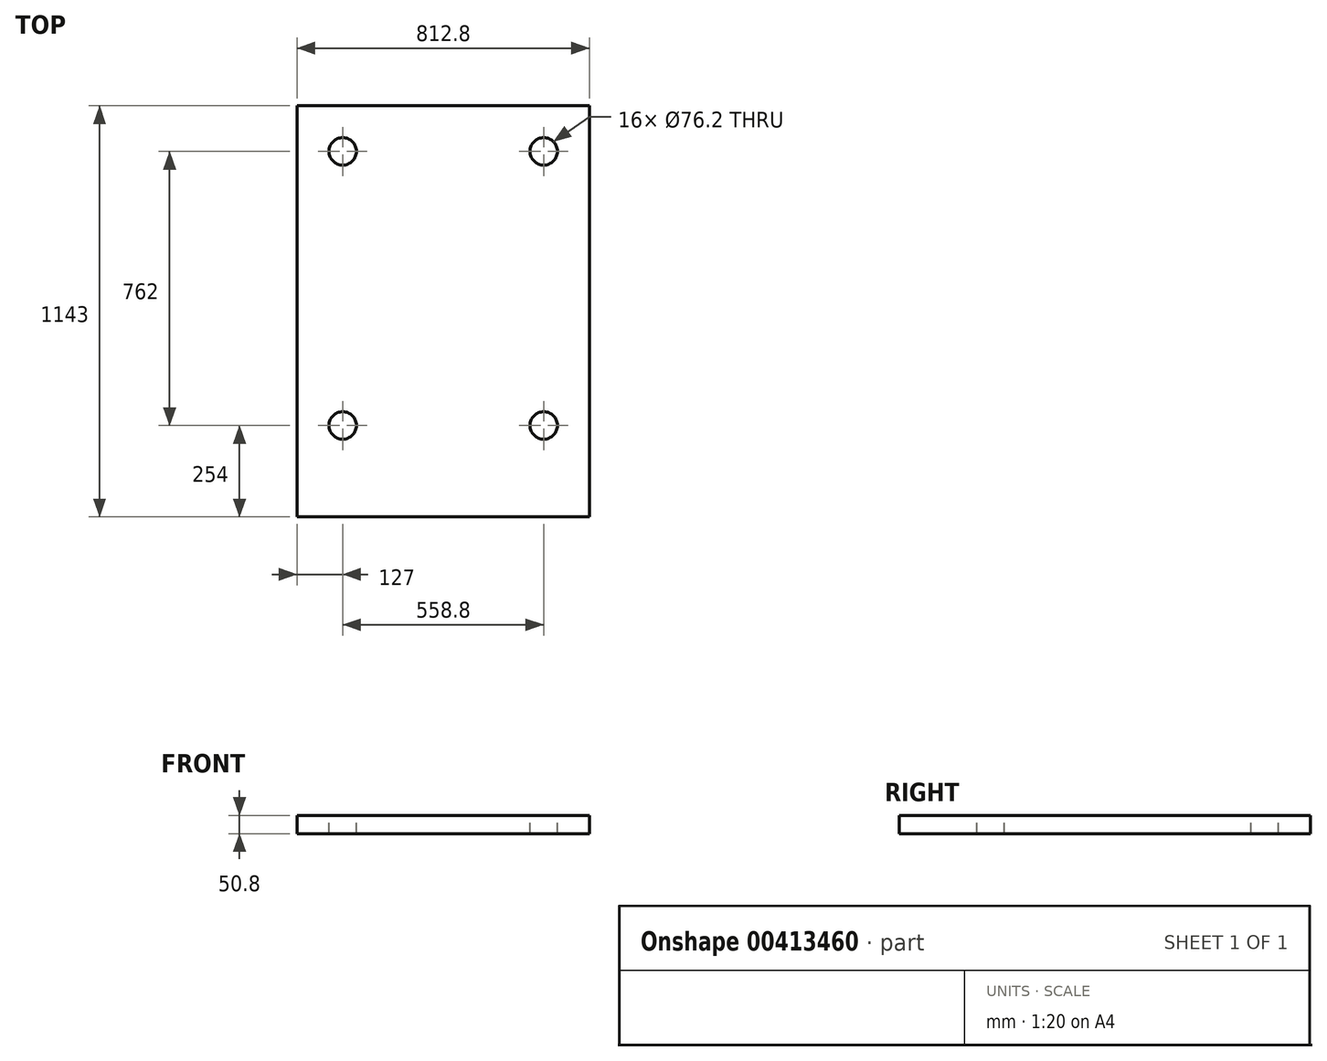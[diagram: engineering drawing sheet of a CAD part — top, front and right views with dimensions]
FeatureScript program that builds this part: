
annotation { "Feature Type Name" : "Feature", "Feature Type Description" : "" }
export const myFeature = defineFeature(function(context is Context, id is Id, definition is map)
    precondition{}
    {
        {
            var Q0;
            Q0=qCreatedBy(makeId("Top.planeOp"),FACE);
            var sketch = newSketch(context, id + "F0", { "sketchPlane" : qUnion([Q0])});
            skLineSegment(sketch, "E0.bottom", {"start": v(0, 0) * mm, "end": v(812.8, 0) * mm});
            skLineSegment(sketch, "E0.top", {"start": v(0, 1143) * mm, "end": v(812.8, 1143) * mm});
            skLineSegment(sketch, "E0.left", {"start": v(0, 0) * mm, "end": v(0, 1143) * mm});
            skLineSegment(sketch, "E0.right", {"start": v(812.8, 0) * mm, "end": v(812.8, 1143) * mm});
            skSolve(sketch);
        }
        {
            var Q0;
            Q0=makeQuery(id+"F0.imprint","IMPRINT",FACE,{"disambiguationData":[TD([[makeQuery(id+"F0.imprint","IMPRINT",EDGE,{"derivedFrom":sQuery(id+"F0.wireOp",EDGE,"E0.bottom")}),1.0]])]});
            extrude(context, id + "F1", {"entities" : qUnion([Q0]), "depth" : 50.8 * mm});
        }
        {
            var Q0;
            Q0=makeQuery(id+"F1.opExtrude","CAP_FACE",FACE,{"disambiguationData":[OSD([sQuery(id+"F0.wireOp",EDGE,"E0.bottom"),sQuery(id+"F0.wireOp",EDGE,"E0.top"),sQuery(id+"F0.wireOp",EDGE,"E0.left"),sQuery(id+"F0.wireOp",EDGE,"E0.right")])],"isStart":false});
            var sketch = newSketch(context, id + "F2", { "sketchPlane" : qUnion([Q0])});
            skCircle(sketch, "E1", {"center": v(685.8, 254) * mm, "radius": 38.1 * mm});
            skCircle(sketch, "E2", {"center": v(127, 254) * mm, "radius": 38.1 * mm});
            skCircle(sketch, "E3", {"center": v(685.8, 1016) * mm, "radius": 38.1 * mm});
            skCircle(sketch, "E4", {"center": v(127, 1016) * mm, "radius": 38.1 * mm});
            skSolve(sketch);
        }
        {
            var Q0;
            Q0 = qSketchRegion(id + "F2", true);
            extrude(context, id + "F3", {"entities" : qUnion([Q0]), "operationType" : NewBodyOperationType.REMOVE, "endBound" : BoundingType.THROUGH_ALL, "oppositeDirection" : true, "depth" : 25.4 * mm});
        }
    });
